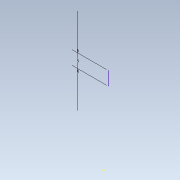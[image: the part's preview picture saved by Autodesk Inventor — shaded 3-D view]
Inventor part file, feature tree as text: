
AUTODESK INVENTOR PART (.ipt)
format: ipt  version: 2021 (Build 250183000, 183)  size: 64,000 bytes
history: native  units: mm
features: sketch x1
ambient origin geometry x8: Origin, YZ Plane, XZ Plane, XY Plane, X Axis, Y Axis, Z Axis, Center Point
feature tree (1):
  sketch  "Sketch1"  dims[d0=5.0mm]
